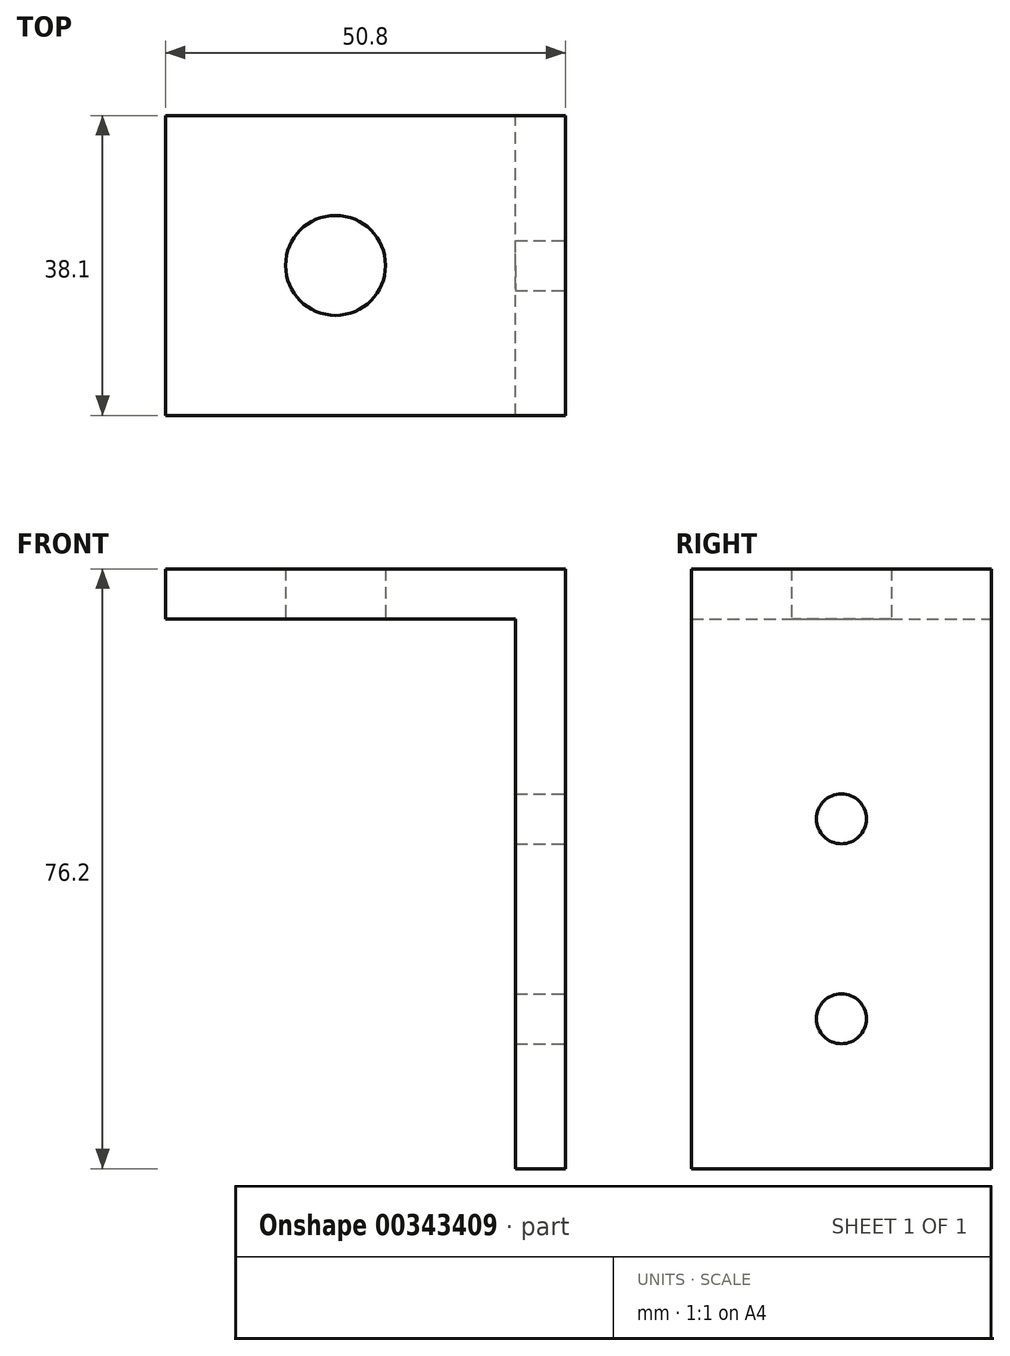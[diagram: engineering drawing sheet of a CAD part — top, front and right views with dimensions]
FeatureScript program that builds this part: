
annotation { "Feature Type Name" : "Feature", "Feature Type Description" : "" }
export const myFeature = defineFeature(function(context is Context, id is Id, definition is map)
    precondition{}
    {
        {
            var Q0;
            Q0=qCreatedBy(makeId("Front.planeOp"),FACE);
            var sketch = newSketch(context, id + "F0", { "sketchPlane" : qUnion([Q0])});
            skLineSegment(sketch, "E0", {"start": v(0, 0) * mm, "end": v(0, 69.85) * mm});
            skLineSegment(sketch, "E1", {"start": v(0, 69.85) * mm, "end": v(-44.45, 69.85) * mm});
            skLineSegment(sketch, "E2", {"start": v(-44.45, 69.85) * mm, "end": v(-44.45, 76.2) * mm});
            skLineSegment(sketch, "E3", {"start": v(-44.45, 76.2) * mm, "end": v(6.35, 76.2) * mm});
            skLineSegment(sketch, "E4", {"start": v(6.35, 76.2) * mm, "end": v(6.35, 0) * mm});
            skLineSegment(sketch, "E5", {"start": v(6.35, 0) * mm, "end": v(0, 0) * mm});
            skSolve(sketch);
        }
        {
            var Q0;
            Q0=makeQuery(id+"F0.imprint","IMPRINT",FACE,{"disambiguationData":[TD([[makeQuery(id+"F0.imprint","IMPRINT",EDGE,{"derivedFrom":sQuery(id+"F0.wireOp",EDGE,"E0")}),-1.0]])]});
            extrude(context, id + "F1", {"entities" : qUnion([Q0]), "depth" : 38.1 * mm});
        }
        {
            var Q0;
            Q0=makeQuery(id+"F1.opExtrude","SWEPT_FACE",FACE,{"disambiguationData":[OSD([sQuery(id+"F0.wireOp",EDGE,"E4")])]});
            var sketch = newSketch(context, id + "F2", { "sketchPlane" : qUnion([Q0])});
            skCircle(sketch, "E6", {"center": v(-19.05, 44.45) * mm, "radius": 3.18 * mm});
            skLineSegment(sketch, "E7", {"start": v(-19.05, 0) * mm, "end": v(-19.05, 12.87) * mm, "construction": true});
            skCircle(sketch, "E8", {"center": v(-19.05, 19.05) * mm, "radius": 3.18 * mm});
            skSolve(sketch);
        }
        {
            var Q0;
            Q0=makeQuery(id+"F2.imprint","IMPRINT",FACE,{"disambiguationData":[TD([[makeQuery(id+"F2.imprint","IMPRINT",EDGE,{"derivedFrom":sQuery(id+"F2.wireOp",EDGE,"E6")}),1.0]])]});
            var Q1;
            Q1=makeQuery(id+"F2.imprint","IMPRINT",FACE,{"disambiguationData":[TD([[makeQuery(id+"F2.imprint","IMPRINT",EDGE,{"derivedFrom":sQuery(id+"F2.wireOp",EDGE,"E8")}),1.0]])]});
            extrude(context, id + "F3", {"entities" : qUnion([Q0, Q1]), "operationType" : NewBodyOperationType.REMOVE, "oppositeDirection" : true, "depth" : 25.4 * mm});
        }
        {
            var Q0;
            Q0=makeQuery(id+"F1.opExtrude","SWEPT_FACE",FACE,{"disambiguationData":[OSD([sQuery(id+"F0.wireOp",EDGE,"E1")])]});
            var sketch = newSketch(context, id + "F4", { "sketchPlane" : qUnion([Q0])});
            skCircle(sketch, "E9", {"center": v(-22.86, 19.05) * mm, "radius": 6.35 * mm});
            skLineSegment(sketch, "E10", {"start": v(-44.45, 19.05) * mm, "end": v(-33.23, 19.05) * mm, "construction": true});
            skSolve(sketch);
        }
        {
            var Q0;
            Q0=makeQuery(id+"F4.imprint","IMPRINT",FACE,{"disambiguationData":[TD([[makeQuery(id+"F4.imprint","IMPRINT",EDGE,{"derivedFrom":sQuery(id+"F4.wireOp",EDGE,"E9")}),1.0]])]});
            extrude(context, id + "F5", {"entities" : qUnion([Q0]), "operationType" : NewBodyOperationType.REMOVE, "oppositeDirection" : true, "depth" : 25.4 * mm});
        }
    });
